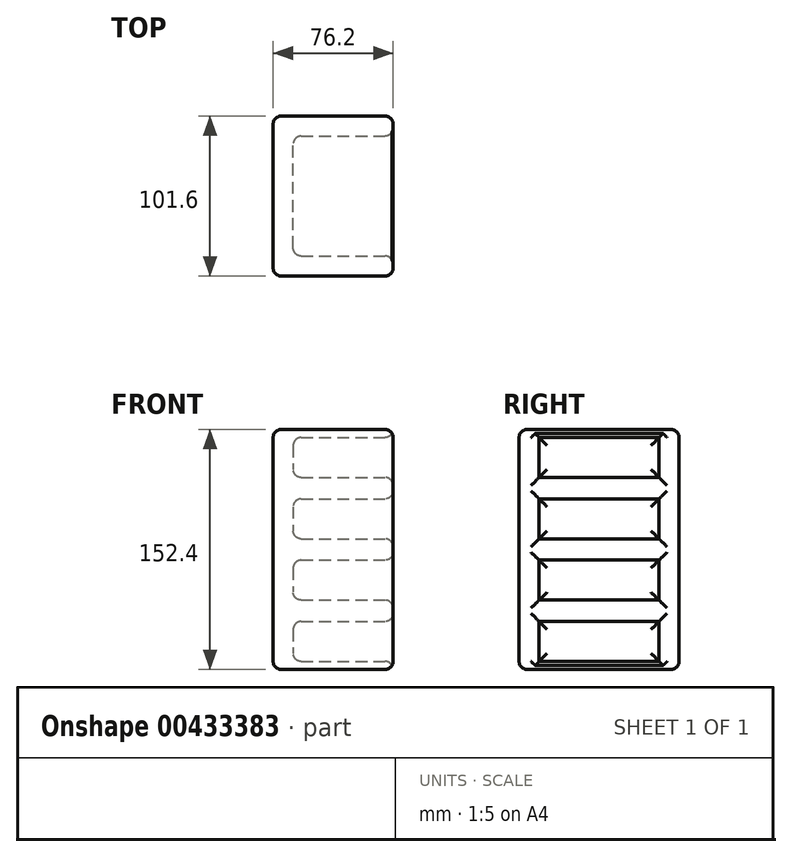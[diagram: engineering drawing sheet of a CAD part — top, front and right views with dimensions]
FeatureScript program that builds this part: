
annotation { "Feature Type Name" : "Feature", "Feature Type Description" : "" }
export const myFeature = defineFeature(function(context is Context, id is Id, definition is map)
    precondition{}
    {
        {
            var Q0;
            Q0=qCreatedBy(makeId("Top.planeOp"),FACE);
            var sketch = newSketch(context, id + "F0", { "sketchPlane" : qUnion([Q0])});
            skLineSegment(sketch, "E0.bottom", {"start": v(-35.15, 70.4) * mm, "end": v(41.05, 70.4) * mm});
            skLineSegment(sketch, "E0.top", {"start": v(-35.15, -31.2) * mm, "end": v(41.05, -31.2) * mm});
            skLineSegment(sketch, "E0.left", {"start": v(-35.15, 70.4) * mm, "end": v(-35.15, -31.2) * mm});
            skLineSegment(sketch, "E0.right", {"start": v(41.05, 70.4) * mm, "end": v(41.05, -31.2) * mm});
            skSolve(sketch);
        }
        {
            var Q0;
            Q0=makeQuery(id+"F0.imprint","IMPRINT",FACE,{"disambiguationData":[TD([[makeQuery(id+"F0.imprint","IMPRINT",EDGE,{"derivedFrom":sQuery(id+"F0.wireOp",EDGE,"E0.bottom")}),-1.0]])]});
            extrude(context, id + "F1", {"entities" : qUnion([Q0]), "depth" : 152.4 * mm});
        }
        {
            var Q0;
            Q0=makeQuery(id+"F1.opExtrude","SWEPT_FACE",FACE,{"disambiguationData":[OSD([sQuery(id+"F0.wireOp",EDGE,"E0.right")])]});
            var sketch = newSketch(context, id + "F2", { "sketchPlane" : qUnion([Q0])});
            skLineSegment(sketch, "E1.bottom", {"start": v(-18.5, 147.32) * mm, "end": v(57.7, 147.32) * mm});
            skLineSegment(sketch, "E1.top", {"start": v(-18.5, 121.92) * mm, "end": v(57.7, 121.92) * mm});
            skLineSegment(sketch, "E1.left", {"start": v(-18.5, 147.32) * mm, "end": v(-18.5, 121.92) * mm});
            skLineSegment(sketch, "E1.right", {"start": v(57.7, 147.32) * mm, "end": v(57.7, 121.92) * mm});
            skLineSegment(sketch, "E2.0.1.0", {"start": v(-18.5, 108.37) * mm, "end": v(57.7, 108.37) * mm});
            skLineSegment(sketch, "E2.0.1.1", {"start": v(-18.5, 108.37) * mm, "end": v(-18.5, 82.97) * mm});
            skLineSegment(sketch, "E2.0.1.2", {"start": v(-18.5, 82.97) * mm, "end": v(57.7, 82.97) * mm});
            skLineSegment(sketch, "E2.0.1.3", {"start": v(57.7, 108.37) * mm, "end": v(57.7, 82.97) * mm});
            skLineSegment(sketch, "E2.0.2.0", {"start": v(-18.5, 69.43) * mm, "end": v(57.7, 69.43) * mm});
            skLineSegment(sketch, "E2.0.2.1", {"start": v(-18.5, 69.43) * mm, "end": v(-18.5, 44.03) * mm});
            skLineSegment(sketch, "E2.0.2.2", {"start": v(-18.5, 44.03) * mm, "end": v(57.7, 44.03) * mm});
            skLineSegment(sketch, "E2.0.2.3", {"start": v(57.7, 69.43) * mm, "end": v(57.7, 44.03) * mm});
            skLineSegment(sketch, "E2.0.3.0", {"start": v(-18.5, 30.48) * mm, "end": v(57.7, 30.48) * mm});
            skLineSegment(sketch, "E2.0.3.1", {"start": v(-18.5, 30.48) * mm, "end": v(-18.5, 5.08) * mm});
            skLineSegment(sketch, "E2.0.3.2", {"start": v(-18.5, 5.08) * mm, "end": v(57.7, 5.08) * mm});
            skLineSegment(sketch, "E2.0.3.3", {"start": v(57.7, 30.48) * mm, "end": v(57.7, 5.08) * mm});
            skLineSegment(sketch, "E2.direction1", {"start": v(-18.5, 147.32) * mm, "end": v(6.9, 147.32) * mm, "construction": true});
            skLineSegment(sketch, "E2.direction2", {"start": v(-18.5, 147.32) * mm, "end": v(-18.5, 108.37) * mm, "construction": true});
            skSolve(sketch);
        }
        {
            var Q0;
            Q0=makeQuery(id+"F2.imprint","IMPRINT",FACE,{"disambiguationData":[TD([[makeQuery(id+"F2.imprint","IMPRINT",EDGE,{"derivedFrom":sQuery(id+"F2.wireOp",EDGE,"E1.bottom")}),-1.0]])]});
            var Q1;
            Q1=makeQuery(id+"F2.imprint","IMPRINT",FACE,{"disambiguationData":[TD([[makeQuery(id+"F2.imprint","IMPRINT",EDGE,{"derivedFrom":sQuery(id+"F2.wireOp",EDGE,"E2.0.1.0")}),-1.0]])]});
            var Q2;
            Q2=makeQuery(id+"F2.imprint","IMPRINT",FACE,{"disambiguationData":[TD([[makeQuery(id+"F2.imprint","IMPRINT",EDGE,{"derivedFrom":sQuery(id+"F2.wireOp",EDGE,"E2.0.2.0")}),-1.0]])]});
            var Q3;
            Q3=makeQuery(id+"F2.imprint","IMPRINT",FACE,{"disambiguationData":[TD([[makeQuery(id+"F2.imprint","IMPRINT",EDGE,{"derivedFrom":sQuery(id+"F2.wireOp",EDGE,"E2.0.3.0")}),-1.0]])]});
            extrude(context, id + "F3", {"entities" : qUnion([Q0, Q1, Q2, Q3]), "operationType" : NewBodyOperationType.REMOVE, "oppositeDirection" : true, "depth" : 63.5 * mm});
        }
        {
            var Q0;
            Q0=makeQuery(id+"F1.opExtrude","SWEPT_FACE",FACE,{"disambiguationData":[OSD([sQuery(id+"F0.wireOp",EDGE,"E0.top")])]});
            var Q1;
            Q1=makeQuery(id+"F1.opExtrude","SWEPT_FACE",FACE,{"disambiguationData":[OSD([sQuery(id+"F0.wireOp",EDGE,"E0.bottom")])]});
            var Q2;
            Q2=makeQuery(id+"F1.opExtrude","CAP_FACE",FACE,{"disambiguationData":[OSD([sQuery(id+"F0.wireOp",EDGE,"E0.bottom"),sQuery(id+"F0.wireOp",EDGE,"E0.top"),sQuery(id+"F0.wireOp",EDGE,"E0.left"),sQuery(id+"F0.wireOp",EDGE,"E0.right")])],"isStart":true});
            var Q3;
            Q3=makeQuery(id+"F1.opExtrude","CAP_FACE",FACE,{"disambiguationData":[OSD([sQuery(id+"F0.wireOp",EDGE,"E0.bottom"),sQuery(id+"F0.wireOp",EDGE,"E0.top"),sQuery(id+"F0.wireOp",EDGE,"E0.left"),sQuery(id+"F0.wireOp",EDGE,"E0.right")])],"isStart":false});
            var Q4;
            Q4=makeQuery(id+"F3.boolean.opBoolean","COPY",FACE,{"derivedFrom":makeQuery(id+"F3.opExtrude","CAP_FACE",FACE,{"disambiguationData":[OSD([sQuery(id+"F2.wireOp",EDGE,"E1.bottom"),sQuery(id+"F2.wireOp",EDGE,"E1.top"),sQuery(id+"F2.wireOp",EDGE,"E1.left"),sQuery(id+"F2.wireOp",EDGE,"E1.right")])],"isStart":false})});
            var Q5;
            Q5=makeQuery(id+"F3.boolean.opBoolean","COPY",FACE,{"derivedFrom":makeQuery(id+"F3.opExtrude","CAP_FACE",FACE,{"disambiguationData":[OSD([sQuery(id+"F2.wireOp",EDGE,"E2.0.1.0"),sQuery(id+"F2.wireOp",EDGE,"E2.0.1.1"),sQuery(id+"F2.wireOp",EDGE,"E2.0.1.2"),sQuery(id+"F2.wireOp",EDGE,"E2.0.1.3")])],"isStart":false})});
            var Q6;
            Q6=makeQuery(id+"F3.boolean.opBoolean","COPY",FACE,{"derivedFrom":makeQuery(id+"F3.opExtrude","CAP_FACE",FACE,{"disambiguationData":[OSD([sQuery(id+"F2.wireOp",EDGE,"E2.0.2.0"),sQuery(id+"F2.wireOp",EDGE,"E2.0.2.1"),sQuery(id+"F2.wireOp",EDGE,"E2.0.2.2"),sQuery(id+"F2.wireOp",EDGE,"E2.0.2.3")])],"isStart":false})});
            var Q7;
            Q7=makeQuery(id+"F3.boolean.opBoolean","COPY",FACE,{"derivedFrom":makeQuery(id+"F3.opExtrude","CAP_FACE",FACE,{"disambiguationData":[OSD([sQuery(id+"F2.wireOp",EDGE,"E2.0.3.0"),sQuery(id+"F2.wireOp",EDGE,"E2.0.3.1"),sQuery(id+"F2.wireOp",EDGE,"E2.0.3.2"),sQuery(id+"F2.wireOp",EDGE,"E2.0.3.3")])],"isStart":false})});
            var Q8;
            Q8=makeQuery(id+"F1.opExtrude","SWEPT_FACE",FACE,{"disambiguationData":[OSD([sQuery(id+"F0.wireOp",EDGE,"E0.right")])]});
            fillet(context, id + "F4", {"entities" : qUnion([Q0, Q1, Q2, Q3, Q4, Q5, Q6, Q7, Q8]), "radius" : 5.08 * mm, "tangentPropagation" : true, "allowEdgeOverflow" : false});
        }
    });
